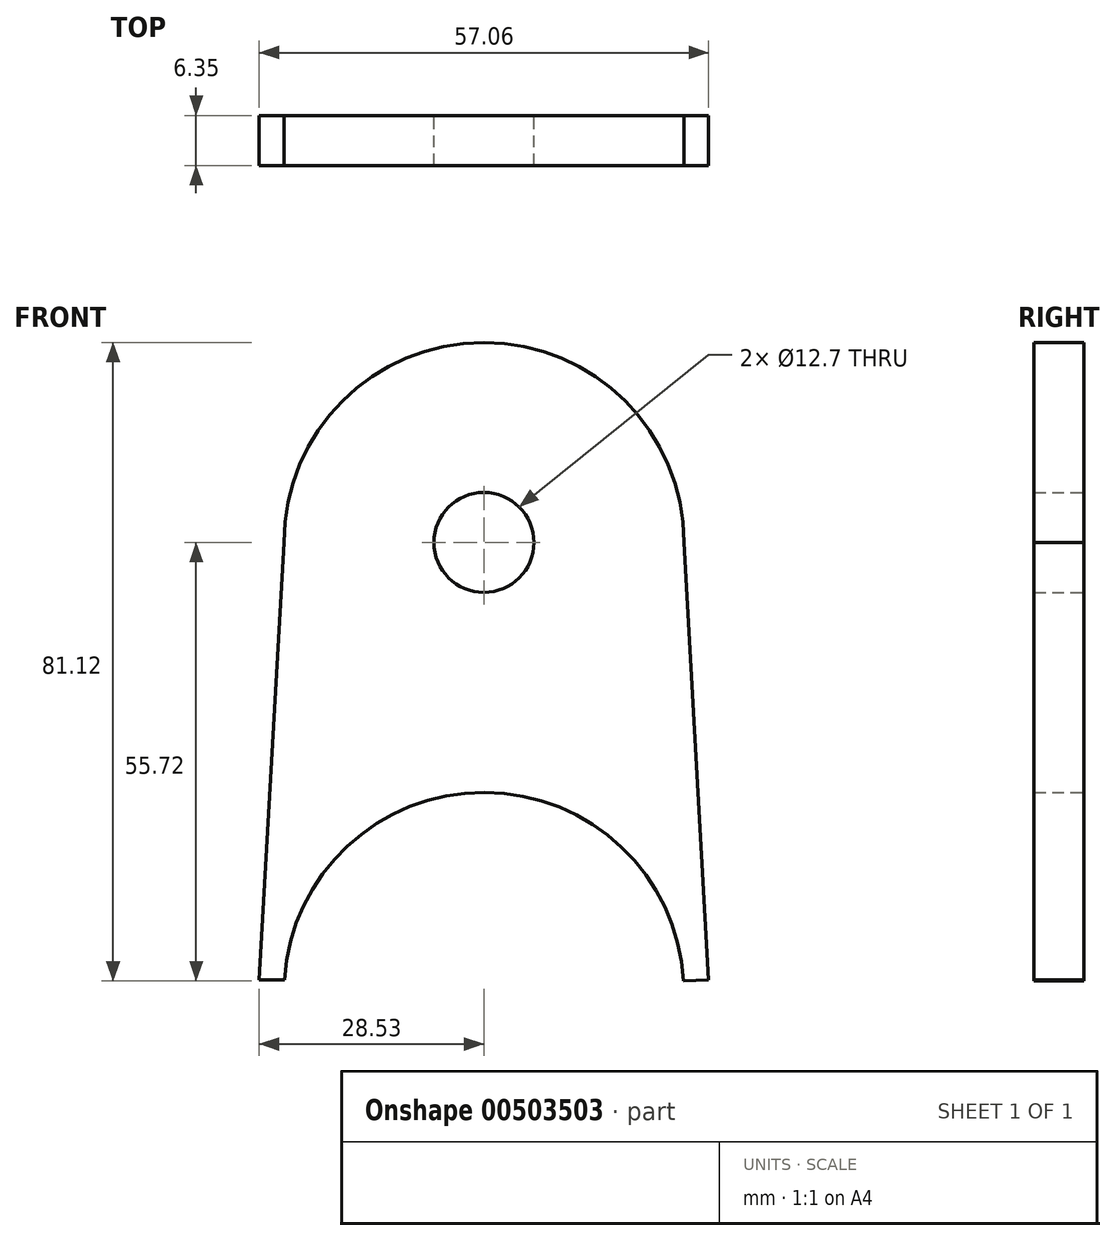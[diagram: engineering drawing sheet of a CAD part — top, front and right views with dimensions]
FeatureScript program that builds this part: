
annotation { "Feature Type Name" : "Feature", "Feature Type Description" : "" }
export const myFeature = defineFeature(function(context is Context, id is Id, definition is map)
    precondition{}
    {
        {
            var Q0;
            Q0=qCreatedBy(makeId("Front.planeOp"),FACE);
            var sketch = newSketch(context, id + "F0", { "sketchPlane" : qUnion([Q0])});
            skArc(sketch, "E0", {"start": v(25.4, 0) * mm, "mid": v(0, 25.4) * mm, "end": v(-25.4, 0) * mm});
            skCircle(sketch, "E1", {"center": v(0, 0) * mm, "radius": 6.35 * mm});
            skPoint(sketch, "E2", {"position": v(0, -57.15) * mm});
            skArc(sketch, "E3", {"start": v(25.36, -55.72) * mm, "mid": v(0.09, -31.75) * mm, "end": v(-25.35, -55.54) * mm});
            skLineSegment(sketch, "E4", {"start": v(-25.4, 0) * mm, "end": v(-28.53, -55.54) * mm});
            skLineSegment(sketch, "E5", {"start": v(25.4, 0) * mm, "end": v(28.53, -55.54) * mm});
            skLineSegment(sketch, "E6", {"start": v(-28.53, -55.54) * mm, "end": v(-25.35, -55.54) * mm});
            skLineSegment(sketch, "E7", {"start": v(28.53, -55.54) * mm, "end": v(25.36, -55.72) * mm});
            skSolve(sketch);
        }
        {
            var Q0;
            Q0 = qSketchRegion(id + "F0", true);
            extrude(context, id + "F1", {"entities" : qUnion([Q0]), "depth" : 6.35 * mm});
        }
    });
